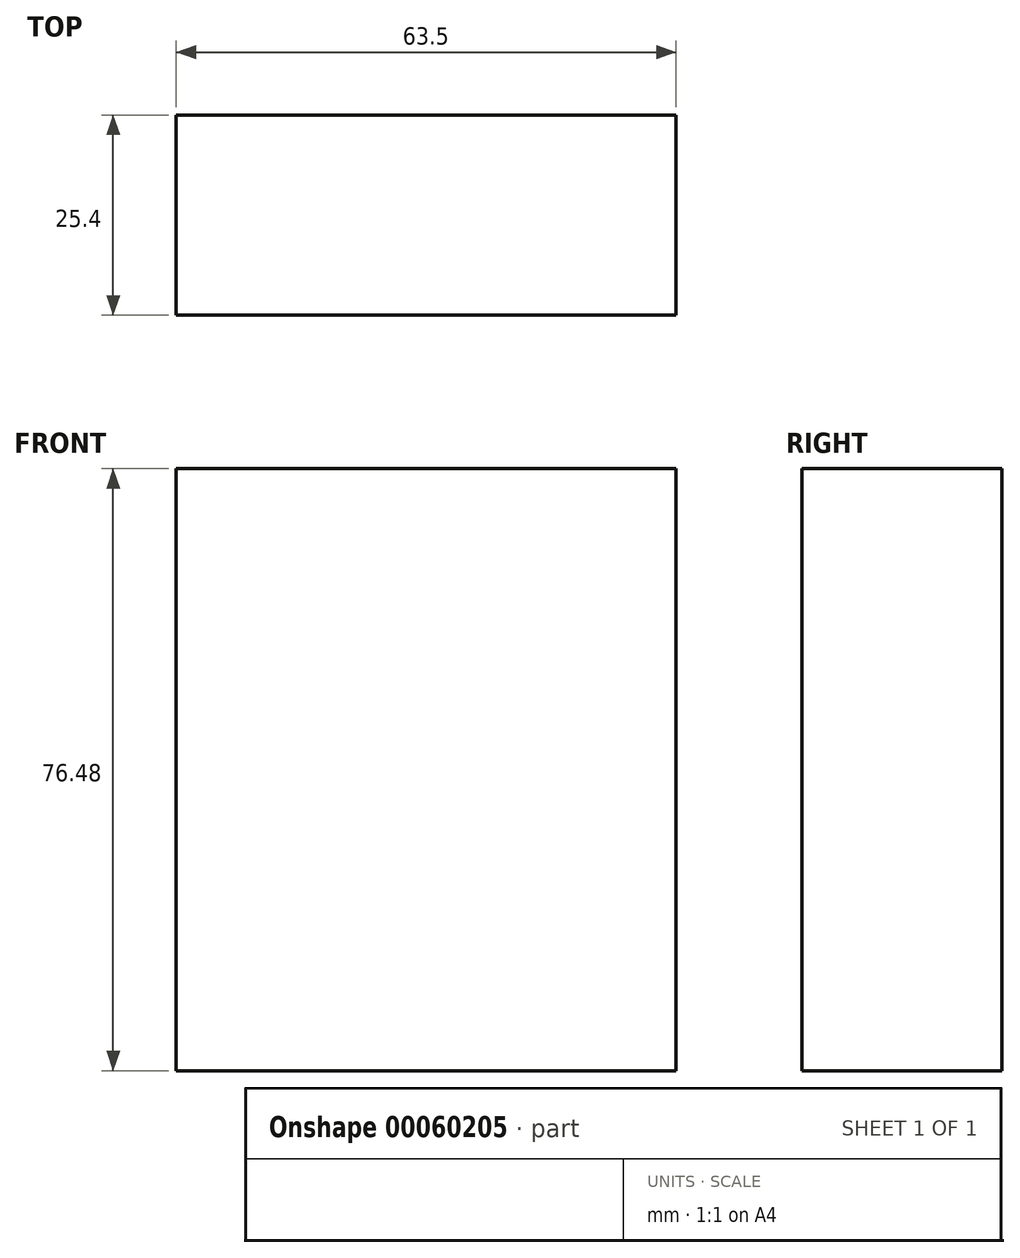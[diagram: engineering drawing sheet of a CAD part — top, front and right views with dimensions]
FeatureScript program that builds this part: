
annotation { "Feature Type Name" : "Feature", "Feature Type Description" : "" }
export const myFeature = defineFeature(function(context is Context, id is Id, definition is map)
    precondition{}
    {
        {
            var Q0;
            Q0=qCreatedBy(makeId("Front.planeOp"),FACE);
            var sketch = newSketch(context, id + "F1", { "sketchPlane" : qUnion([Q0])});
            skLineSegment(sketch, "E0.rect.bottom", {"start": v(31.75, 38.24) * mm, "end": v(-31.75, 38.24) * mm});
            skLineSegment(sketch, "E0.rect.top", {"start": v(31.75, -38.24) * mm, "end": v(-31.75, -38.24) * mm});
            skLineSegment(sketch, "E0.rect.left", {"start": v(31.75, 38.24) * mm, "end": v(31.75, -38.24) * mm});
            skLineSegment(sketch, "E0.rect.right", {"start": v(-31.75, 38.24) * mm, "end": v(-31.75, -38.24) * mm});
            skPoint(sketch, "E0.rect.middle", {"position": v(0, 0) * mm});
            skSolve(sketch);
        }
        {
            var Q0;
            Q0=makeQuery(id+"F1.imprint","IMPRINT",FACE,{"disambiguationData":[TD([[makeQuery(id+"F1.imprint","IMPRINT",EDGE,{"derivedFrom":sQuery(id+"F1.wireOp",EDGE,"E0.rect.bottom")}),1.0]])]});
            extrude(context, id + "F0", {"entities" : qUnion([Q0]), "depth" : 25.4 * mm});
        }
    });
